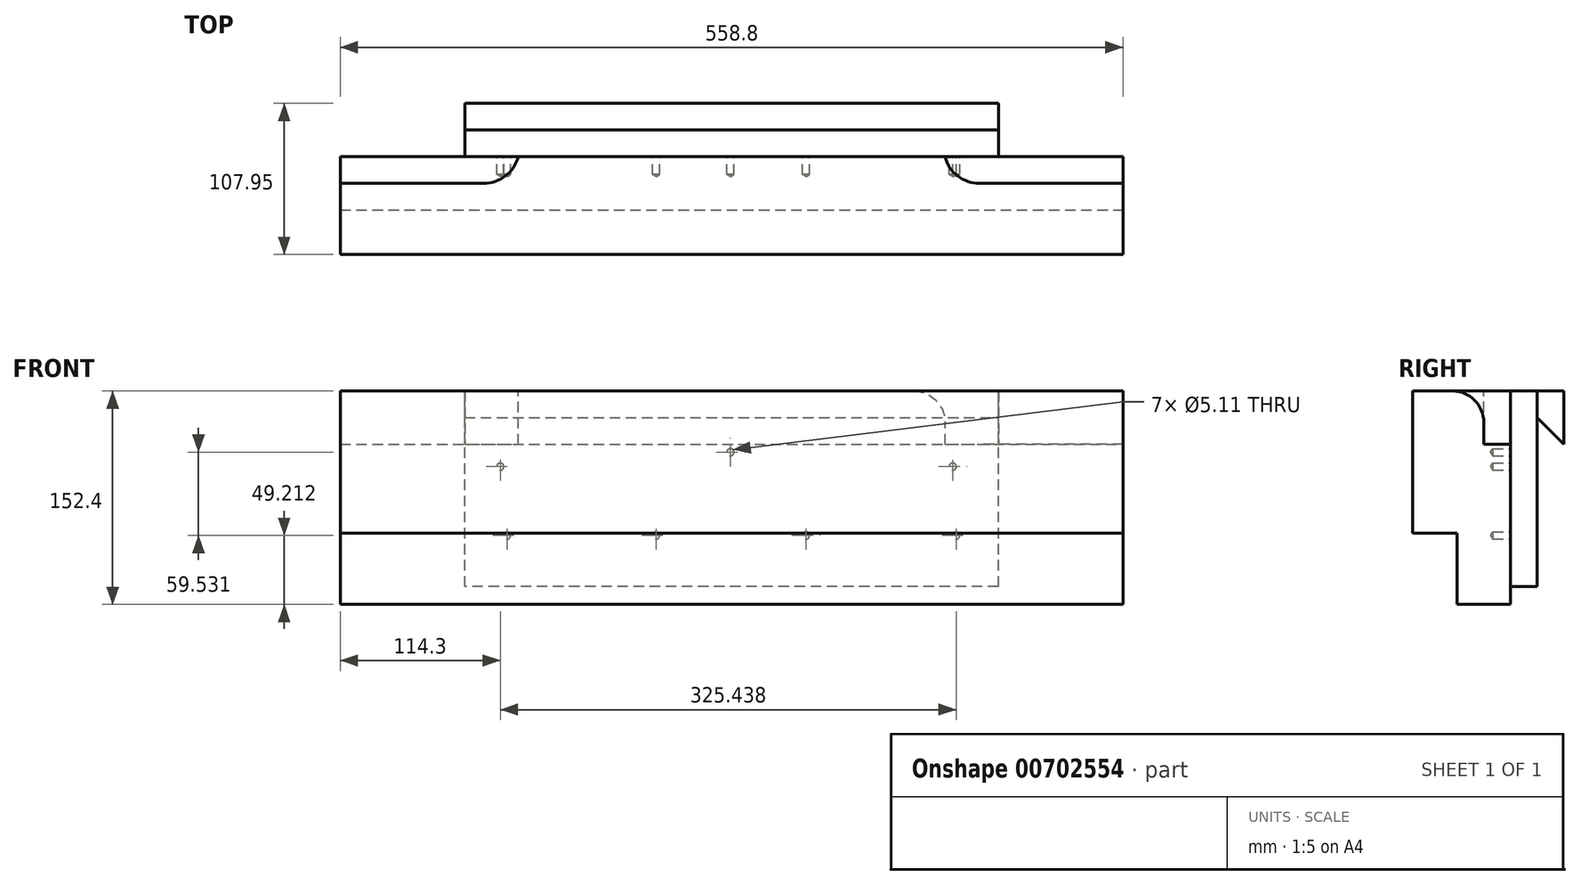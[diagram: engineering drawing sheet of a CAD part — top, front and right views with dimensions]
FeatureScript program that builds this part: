
annotation { "Feature Type Name" : "Feature", "Feature Type Description" : "" }
export const myFeature = defineFeature(function(context is Context, id is Id, definition is map)
    precondition{}
    {
        {
            var Q0;
            Q0=qCreatedBy(makeId("Front.planeOp"),FACE);
            var sketch = newSketch(context, id + "F0", { "sketchPlane" : qUnion([Q0])});
            skLineSegment(sketch, "E0.bottom", {"start": v(0, 0) * mm, "end": v(558.8, 0) * mm});
            skLineSegment(sketch, "E0.top", {"start": v(0, 152.4) * mm, "end": v(558.8, 152.4) * mm});
            skLineSegment(sketch, "E0.left", {"start": v(0, 0) * mm, "end": v(0, 152.4) * mm});
            skLineSegment(sketch, "E0.right", {"start": v(558.8, 0) * mm, "end": v(558.8, 152.4) * mm});
            skSolve(sketch);
        }
        {
            var Q0;
            Q0 = qSketchRegion(id + "F0", true);
            extrude(context, id + "F1", {"entities" : qUnion([Q0]), "depth" : 69.85 * mm, "offsetDistance" : 25.4 * mm});
        }
        {
            var Q0;
            Q0=makeQuery(id+"F1.opExtrude","CAP_FACE",FACE,{"disambiguationData":[OSD([sQuery(id+"F0.wireOp",EDGE,"E0.bottom"),sQuery(id+"F0.wireOp",EDGE,"E0.top"),sQuery(id+"F0.wireOp",EDGE,"E0.left"),sQuery(id+"F0.wireOp",EDGE,"E0.right")])],"isStart":false});
            var sketch = newSketch(context, id + "F2", { "sketchPlane" : qUnion([Q0])});
            skLineSegment(sketch, "E1.bottom", {"start": v(0, 0) * mm, "end": v(558.8, 0) * mm});
            skLineSegment(sketch, "E1.top", {"start": v(0, 50.8) * mm, "end": v(558.8, 50.8) * mm});
            skLineSegment(sketch, "E1.left", {"start": v(0, 0) * mm, "end": v(0, 50.8) * mm});
            skLineSegment(sketch, "E1.right", {"start": v(558.8, 0) * mm, "end": v(558.8, 50.8) * mm});
            skSolve(sketch);
        }
        {
            var Q0;
            Q0 = qSketchRegion(id + "F2", true);
            extrude(context, id + "F3", {"entities" : qUnion([Q0]), "operationType" : NewBodyOperationType.REMOVE, "oppositeDirection" : true, "depth" : 31.75 * mm, "offsetDistance" : 25.4 * mm});
        }
        {
            var Q0;
            Q0=makeQuery(id+"F1.opExtrude","SWEPT_FACE",FACE,{"disambiguationData":[OSD([sQuery(id+"F0.wireOp",EDGE,"E0.top")])]});
            var sketch = newSketch(context, id + "F4", { "sketchPlane" : qUnion([Q0])});
            skLineSegment(sketch, "E2.bottom", {"start": v(0, 0) * mm, "end": v(127, 0) * mm});
            skLineSegment(sketch, "E2.top", {"start": v(0, -19.05) * mm, "end": v(127, -19.05) * mm});
            skLineSegment(sketch, "E2.left", {"start": v(0, 0) * mm, "end": v(0, -19.05) * mm});
            skLineSegment(sketch, "E2.right", {"start": v(127, 0) * mm, "end": v(127, -19.05) * mm});
            skLineSegment(sketch, "E3", {"start": v(279.4, 0) * mm, "end": v(279.4, -69.85) * mm, "construction": true});
            skLineSegment(sketch, "E4.MirrorCS", {"start": v(558.8, -19.05) * mm, "end": v(431.8, -19.05) * mm});
            skLineSegment(sketch, "E5.MirrorCS", {"start": v(558.8, 0) * mm, "end": v(558.8, -19.05) * mm});
            skLineSegment(sketch, "E6.MirrorCS", {"start": v(558.8, 0) * mm, "end": v(431.8, 0) * mm});
            skLineSegment(sketch, "E7.MirrorCS", {"start": v(431.8, 0) * mm, "end": v(431.8, -19.05) * mm});
            skSolve(sketch);
        }
        {
            var Q0;
            Q0 = qSketchRegion(id + "F4", true);
            extrude(context, id + "F5", {"entities" : qUnion([Q0]), "operationType" : NewBodyOperationType.REMOVE, "oppositeDirection" : true, "depth" : 38.1 * mm, "offsetDistance" : 25.4 * mm});
        }
        {
            var Q0;
            Q0=makeQuery(id+"F5.boolean.opBoolean","COPY",EDGE,{"derivedFrom":makeQuery(id+"F5.opExtrude","SWEPT_EDGE",EDGE,{"disambiguationData":[OSD([sQuery(id+"F4.wireOp",EDGE,"E2.top"),sQuery(id+"F4.wireOp",EDGE,"E2.right")])]})});
            var Q1;
            Q1=makeQuery(id+"F5.boolean.opBoolean","COPY",EDGE,{"derivedFrom":makeQuery(id+"F5.opExtrude","SWEPT_EDGE",EDGE,{"disambiguationData":[OSD([sQuery(id+"F4.wireOp",EDGE,"E4.MirrorCS"),sQuery(id+"F4.wireOp",EDGE,"E7.MirrorCS")])]})});
            fillet(context, id + "F6", {"entities" : qUnion([Q0, Q1]), "tangentPropagation" : true, "radius" : 25.4 * mm, "defaultsChanged" : true, "vertexSettings" : [], "allowEdgeOverflow" : false});
        }
        {
            var Q0;
            Q0=makeQuery(id+"F5.boolean.opBoolean","COPY",EDGE,{"derivedFrom":makeQuery(id+"F5.opExtrude","CAP_EDGE",EDGE,{"disambiguationData":[OSD([sQuery(id+"F4.wireOp",EDGE,"E2.top")])],"isStart":true})});
            var Q1;
            Q1=makeQuery(id+"F6.opFillet","BLEND_EDGE",EDGE,{"blendedFrom":[makeQuery(id+"F5.boolean.opBoolean","COPY",EDGE,{"derivedFrom":makeQuery(id+"F5.opExtrude","SWEPT_EDGE",EDGE,{"disambiguationData":[OSD([sQuery(id+"F4.wireOp",EDGE,"E4.MirrorCS"),sQuery(id+"F4.wireOp",EDGE,"E7.MirrorCS")])]})}),makeQuery(id+"F1.opExtrude","SWEPT_FACE",FACE,{"disambiguationData":[OSD([sQuery(id+"F0.wireOp",EDGE,"E0.top")])]})],"blendedInto":[makeQuery(id+"F1.opExtrude","SWEPT_FACE",FACE,{"disambiguationData":[OSD([sQuery(id+"F0.wireOp",EDGE,"E0.top")])]})]});
            fillet(context, id + "F7", {"entities" : qUnion([Q0, Q1]), "tangentPropagation" : true, "radius" : 22.22 * mm, "defaultsChanged" : true, "vertexSettings" : [], "allowEdgeOverflow" : false});
        }
        {
            var Q0;
            Q0=makeQuery(id+"F1.opExtrude","CAP_FACE",FACE,{"disambiguationData":[OSD([sQuery(id+"F0.wireOp",EDGE,"E0.bottom"),sQuery(id+"F0.wireOp",EDGE,"E0.top"),sQuery(id+"F0.wireOp",EDGE,"E0.left"),sQuery(id+"F0.wireOp",EDGE,"E0.right")])],"isStart":true});
            var sketch = newSketch(context, id + "F8", { "sketchPlane" : qUnion([Q0])});
            skPoint(sketch, "E8", {"position": v(-439.74, 49.21) * mm});
            skPoint(sketch, "E9", {"position": v(-332.58, 49.21) * mm});
            skPoint(sketch, "E10", {"position": v(-225.42, 49.21) * mm});
            skPoint(sketch, "E11", {"position": v(-119.06, 49.21) * mm});
            skPoint(sketch, "E12", {"position": v(-437.36, 98.43) * mm});
            skPoint(sketch, "E13", {"position": v(-278.6, 108.74) * mm});
            skPoint(sketch, "E14", {"position": v(-114.3, 98.43) * mm});
            skSolve(sketch);
        }
        {
            var Q0;
            Q0=sQuery(id+"F8.wireOp",VERTEX,"E8");
            var Q1;
            Q1=sQuery(id+"F8.wireOp",VERTEX,"E12");
            var Q2;
            Q2=sQuery(id+"F8.wireOp",VERTEX,"E9");
            var Q3;
            Q3=sQuery(id+"F8.wireOp",VERTEX,"E13");
            var Q4;
            Q4=sQuery(id+"F8.wireOp",VERTEX,"E10");
            var Q5;
            Q5=sQuery(id+"F8.wireOp",VERTEX,"E11");
            var Q6;
            Q6=sQuery(id+"F8.wireOp",VERTEX,"E14");
            var Q7;
            Q7=makeQuery(id+"F1.opExtrude","SWEPT_BODY",BODY,{"disambiguationData":[OSD([sQuery(id+"F0.wireOp",EDGE,"E0.bottom"),sQuery(id+"F0.wireOp",EDGE,"E0.top"),sQuery(id+"F0.wireOp",EDGE,"E0.left"),sQuery(id+"F0.wireOp",EDGE,"E0.right")])]});
            hole(context, id + "F9", {"style" : HoleStyle.SIMPLE, "endStyle" : HoleEndStyle.BLIND, "standardTappedOrClearance" : lookupTablePath({ "fit" : "Free", "standard" : "ANSI", "size" : "#10", "type" : "Clearance" }), "standardBlindInLast" : lookupTablePath({ "fit" : "Free", "standard" : "ANSI", "engagement" : "75%", "pitch" : "24 tpi", "size" : "#10", "type" : "Clearance & tapped" }), "holeDiameter" : 5.1 * mm, "majorDiameter" : 6.35 * mm, "holeDepth" : 12.7 * mm, "isTappedThrough" : true, "tappedDepth" : 12.7 * mm, "tapClearance" : 3, "locations" : qUnion([Q0, Q1, Q2, Q3, Q4, Q5, Q6]), "scope" : qUnion([Q7])});
        }
        {
            var Q0;
            Q0=makeQuery(id+"F1.opExtrude","CAP_FACE",FACE,{"disambiguationData":[OSD([sQuery(id+"F0.wireOp",EDGE,"E0.bottom"),sQuery(id+"F0.wireOp",EDGE,"E0.top"),sQuery(id+"F0.wireOp",EDGE,"E0.left"),sQuery(id+"F0.wireOp",EDGE,"E0.right")])],"isStart":true});
            var sketch = newSketch(context, id + "F10", { "sketchPlane" : qUnion([Q0])});
            skLineSegment(sketch, "E15.bottom", {"start": v(-469.9, 12.7) * mm, "end": v(-88.9, 12.7) * mm});
            skLineSegment(sketch, "E15.top", {"start": v(-469.9, 152.4) * mm, "end": v(-88.9, 152.4) * mm});
            skLineSegment(sketch, "E15.left", {"start": v(-469.9, 12.7) * mm, "end": v(-469.9, 152.4) * mm});
            skLineSegment(sketch, "E15.right", {"start": v(-88.9, 12.7) * mm, "end": v(-88.9, 152.4) * mm});
            skLineSegment(sketch, "E16", {"start": v(-279.4, 152.4) * mm, "end": v(-279.4, 0) * mm, "construction": true});
            skPoint(sketch, "E17", {"position": v(-279.4, 152.4) * mm});
            skSolve(sketch);
        }
        {
            var Q0;
            Q0 = qSketchRegion(id + "F10", true);
            extrude(context, id + "F11", {"entities" : qUnion([Q0]), "depth" : 19.05 * mm, "offsetDistance" : 25.4 * mm});
        }
        {
            var Q0;
            Q0=makeQuery(id+"F11.opExtrude","SWEPT_FACE",FACE,{"disambiguationData":[OSD([sQuery(id+"F10.wireOp",EDGE,"E15.left")])]});
            var sketch = newSketch(context, id + "F12", { "sketchPlane" : qUnion([Q0])});
            skLineSegment(sketch, "E18.bottom", {"start": v(19.05, 152.4) * mm, "end": v(38.1, 152.4) * mm});
            skLineSegment(sketch, "E18.left", {"start": v(19.05, 152.4) * mm, "end": v(19.05, 133.35) * mm});
            skLineSegment(sketch, "E18.right", {"start": v(38.1, 152.4) * mm, "end": v(38.1, 114.3) * mm});
            skLineSegment(sketch, "E19", {"start": v(38.1, 114.3) * mm, "end": v(19.05, 133.35) * mm});
            skSolve(sketch);
        }
        {
            var Q0;
            Q0=makeQuery(id+"F12.imprint","IMPRINT",FACE,{"disambiguationData":[TD([[makeQuery(id+"F12.imprint","IMPRINT",EDGE,{"derivedFrom":sQuery(id+"F12.wireOp",EDGE,"E18.bottom")}),-1.0]])]});
            extrude(context, id + "F13", {"entities" : qUnion([Q0]), "oppositeDirection" : true, "depth" : 381 * mm, "offsetDistance" : 25.4 * mm});
        }
    });
